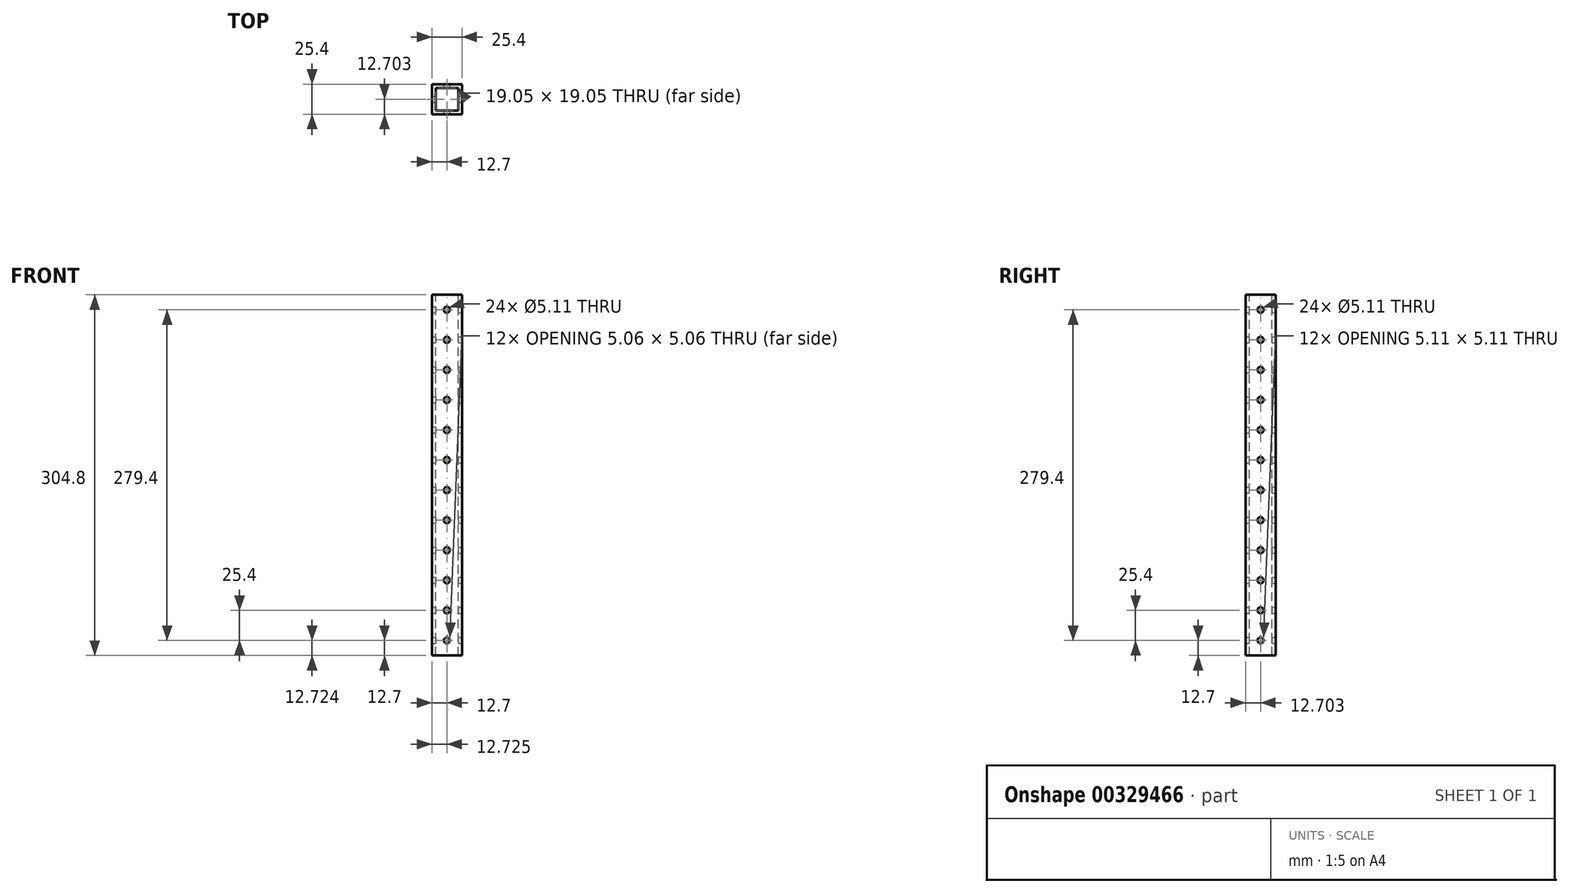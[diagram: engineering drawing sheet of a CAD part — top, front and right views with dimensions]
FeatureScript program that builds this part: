
annotation { "Feature Type Name" : "Feature", "Feature Type Description" : "" }
export const myFeature = defineFeature(function(context is Context, id is Id, definition is map)
    precondition{}
    {
        {
            var Q0;
            Q0=qCreatedBy(makeId("Right.planeOp"),FACE);
            var sketch = newSketch(context, id + "F0", { "sketchPlane" : qUnion([Q0])});
            skLineSegment(sketch, "E0.bottom", {"start": v(-26.89, 312.65) * mm, "end": v(-1.49, 312.65) * mm});
            skLineSegment(sketch, "E0.top", {"start": v(-26.89, 7.85) * mm, "end": v(-1.49, 7.85) * mm});
            skLineSegment(sketch, "E0.left", {"start": v(-26.89, 312.65) * mm, "end": v(-26.89, 7.85) * mm});
            skLineSegment(sketch, "E0.right", {"start": v(-1.49, 312.65) * mm, "end": v(-1.49, 7.85) * mm});
            skSolve(sketch);
        }
        {
            var Q0;
            Q0 = qSketchRegion(id + "F0", true);
            extrude(context, id + "F1", {"entities" : qUnion([Q0]), "depth" : 25.4 * mm});
        }
        {
            var Q0;
            Q0=makeQuery(id+"F1.opExtrude","SWEPT_FACE",FACE,{"disambiguationData":[OSD([sQuery(id+"F0.wireOp",EDGE,"E0.bottom")])]});
            var sketch = newSketch(context, id + "F2", { "sketchPlane" : qUnion([Q0])});
            skLineSegment(sketch, "E1.bottom", {"start": v(3.17, -4.66) * mm, "end": v(22.23, -4.66) * mm});
            skLineSegment(sketch, "E1.top", {"start": v(3.18, -23.71) * mm, "end": v(22.23, -23.71) * mm});
            skLineSegment(sketch, "E1.left", {"start": v(3.17, -4.66) * mm, "end": v(3.18, -23.71) * mm});
            skLineSegment(sketch, "E1.right", {"start": v(22.23, -4.66) * mm, "end": v(22.23, -23.71) * mm});
            skSolve(sketch);
        }
        {
            var Q0;
            Q0 = qSketchRegion(id + "F2", true);
            extrude(context, id + "F3", {"entities" : qUnion([Q0]), "operationType" : NewBodyOperationType.REMOVE, "oppositeDirection" : true, "depth" : 304.8 * mm});
        }
        {
            var Q0;
            Q0=makeQuery(id+"F1.opExtrude","CAP_FACE",FACE,{"disambiguationData":[OSD([sQuery(id+"F0.wireOp",EDGE,"E0.bottom"),sQuery(id+"F0.wireOp",EDGE,"E0.top"),sQuery(id+"F0.wireOp",EDGE,"E0.left"),sQuery(id+"F0.wireOp",EDGE,"E0.right")])],"isStart":false});
            var sketch = newSketch(context, id + "F4", { "sketchPlane" : qUnion([Q0])});
            skCircle(sketch, "E2", {"center": v(-14.19, 299.95) * mm, "radius": 2.55 * mm});
            skCircle(sketch, "E3.0.1.0", {"center": v(-14.19, 274.55) * mm, "radius": 2.55 * mm});
            skCircle(sketch, "E3.0.2.0", {"center": v(-14.19, 249.15) * mm, "radius": 2.55 * mm});
            skCircle(sketch, "E3.0.3.0", {"center": v(-14.19, 223.75) * mm, "radius": 2.55 * mm});
            skCircle(sketch, "E3.0.4.0", {"center": v(-14.19, 198.35) * mm, "radius": 2.55 * mm});
            skCircle(sketch, "E3.0.5.0", {"center": v(-14.19, 172.95) * mm, "radius": 2.55 * mm});
            skCircle(sketch, "E3.0.6.0", {"center": v(-14.19, 147.55) * mm, "radius": 2.55 * mm});
            skCircle(sketch, "E3.0.7.0", {"center": v(-14.19, 122.15) * mm, "radius": 2.55 * mm});
            skCircle(sketch, "E3.0.8.0", {"center": v(-14.19, 96.75) * mm, "radius": 2.55 * mm});
            skCircle(sketch, "E3.0.9.0", {"center": v(-14.19, 71.35) * mm, "radius": 2.55 * mm});
            skCircle(sketch, "E3.0.10.0", {"center": v(-14.19, 45.95) * mm, "radius": 2.55 * mm});
            skCircle(sketch, "E3.0.11.0", {"center": v(-14.19, 20.55) * mm, "radius": 2.55 * mm});
            skLineSegment(sketch, "E3.direction1", {"start": v(-14.19, 299.95) * mm, "end": v(11.21, 299.95) * mm, "construction": true});
            skLineSegment(sketch, "E3.direction2", {"start": v(-14.19, 299.95) * mm, "end": v(-14.19, 274.55) * mm, "construction": true});
            skSolve(sketch);
        }
        {
            var Q0;
            Q0=sQuery(id+"F4.wireOp",VERTEX,"E3.0.11.0.center");
            var Q1;
            Q1=sQuery(id+"F4.wireOp",VERTEX,"E3.0.8.0.center");
            var Q2;
            Q2=sQuery(id+"F4.wireOp",VERTEX,"E3.0.7.0.center");
            var Q3;
            Q3=sQuery(id+"F4.wireOp",VERTEX,"E3.0.6.0.center");
            var Q4;
            Q4=sQuery(id+"F4.wireOp",VERTEX,"E3.0.10.0.center");
            var Q5;
            Q5=sQuery(id+"F4.wireOp",VERTEX,"E3.0.9.0.center");
            var Q6;
            Q6=sQuery(id+"F4.wireOp",VERTEX,"E3.0.5.0.center");
            var Q7;
            Q7=sQuery(id+"F4.wireOp",VERTEX,"E3.direction1.start");
            var Q8;
            Q8=sQuery(id+"F4.wireOp",VERTEX,"E3.0.4.0.center");
            var Q9;
            Q9=sQuery(id+"F4.wireOp",VERTEX,"E3.0.3.0.center");
            var Q10;
            Q10=sQuery(id+"F4.wireOp",VERTEX,"E3.0.2.0.center");
            var Q11;
            Q11=sQuery(id+"F4.wireOp",VERTEX,"E3.0.1.0.center");
            var Q12;
            Q12=sQuery(id+"F4.wireOp",VERTEX,"E3.direction1.end");
            var Q13;
            Q13=makeQuery(id+"F1.opExtrude","SWEPT_BODY",BODY,{"disambiguationData":[OSD([sQuery(id+"F0.wireOp",EDGE,"E0.bottom"),sQuery(id+"F0.wireOp",EDGE,"E0.top"),sQuery(id+"F0.wireOp",EDGE,"E0.left"),sQuery(id+"F0.wireOp",EDGE,"E0.right")])]});
            hole(context, id + "F5", {"style" : HoleStyle.SIMPLE, "endStyle" : HoleEndStyle.BLIND, "holeDiameter" : 5.1 * mm, "holeDepth" : 25.4 * mm, "tappedDepth" : 12.7 * mm, "tapClearance" : 3, "startFromSketch" : true, "locations" : qUnion([Q0, Q1, Q2, Q3, Q4, Q5, Q6, Q7, Q8, Q9, Q10, Q11, Q12]), "scope" : qUnion([Q13])});
        }
        {
            var Q0;
            Q0=makeQuery(id+"F1.opExtrude","SWEPT_FACE",FACE,{"disambiguationData":[OSD([sQuery(id+"F0.wireOp",EDGE,"E0.right")])]});
            var sketch = newSketch(context, id + "F6", { "sketchPlane" : qUnion([Q0])});
            skCircle(sketch, "E4", {"center": v(-12.7, 299.95) * mm, "radius": 2.55 * mm});
            skCircle(sketch, "E5.0.1.0", {"center": v(-12.7, 274.55) * mm, "radius": 2.55 * mm});
            skCircle(sketch, "E5.0.2.0", {"center": v(-12.7, 249.15) * mm, "radius": 2.55 * mm});
            skCircle(sketch, "E5.0.3.0", {"center": v(-12.7, 223.75) * mm, "radius": 2.55 * mm});
            skCircle(sketch, "E5.0.4.0", {"center": v(-12.7, 198.35) * mm, "radius": 2.55 * mm});
            skCircle(sketch, "E5.0.5.0", {"center": v(-12.7, 172.95) * mm, "radius": 2.55 * mm});
            skCircle(sketch, "E5.0.6.0", {"center": v(-12.7, 147.55) * mm, "radius": 2.55 * mm});
            skCircle(sketch, "E5.0.7.0", {"center": v(-12.7, 122.15) * mm, "radius": 2.55 * mm});
            skCircle(sketch, "E5.0.8.0", {"center": v(-12.7, 96.75) * mm, "radius": 2.55 * mm});
            skCircle(sketch, "E5.0.9.0", {"center": v(-12.7, 71.35) * mm, "radius": 2.55 * mm});
            skCircle(sketch, "E5.0.10.0", {"center": v(-12.7, 45.95) * mm, "radius": 2.55 * mm});
            skCircle(sketch, "E5.0.11.0", {"center": v(-12.7, 20.55) * mm, "radius": 2.55 * mm});
            skLineSegment(sketch, "E5.direction1", {"start": v(-12.7, 299.95) * mm, "end": v(12.7, 299.95) * mm, "construction": true});
            skLineSegment(sketch, "E5.direction2", {"start": v(-12.7, 299.95) * mm, "end": v(-12.7, 274.55) * mm, "construction": true});
            skSolve(sketch);
        }
        {
            var Q0;
            Q0=sQuery(id+"F6.wireOp",VERTEX,"E5.0.11.0.center");
            var Q1;
            Q1=sQuery(id+"F6.wireOp",VERTEX,"E5.0.9.0.center");
            var Q2;
            Q2=sQuery(id+"F6.wireOp",VERTEX,"E5.0.10.0.center");
            var Q3;
            Q3=sQuery(id+"F6.wireOp",VERTEX,"E5.direction1.start");
            var Q4;
            Q4=sQuery(id+"F6.wireOp",VERTEX,"E5.0.2.0.center");
            var Q5;
            Q5=sQuery(id+"F6.wireOp",VERTEX,"E5.0.1.0.center");
            var Q6;
            Q6=sQuery(id+"F6.wireOp",VERTEX,"E5.0.7.0.center");
            var Q7;
            Q7=sQuery(id+"F6.wireOp",VERTEX,"E5.0.8.0.center");
            var Q8;
            Q8=sQuery(id+"F6.wireOp",VERTEX,"E5.0.5.0.center");
            var Q9;
            Q9=sQuery(id+"F6.wireOp",VERTEX,"E5.0.6.0.center");
            var Q10;
            Q10=sQuery(id+"F6.wireOp",VERTEX,"E5.0.3.0.center");
            var Q11;
            Q11=sQuery(id+"F6.wireOp",VERTEX,"E5.0.4.0.center");
            var Q12;
            Q12=makeQuery(id+"F1.opExtrude","SWEPT_BODY",BODY,{"disambiguationData":[OSD([sQuery(id+"F0.wireOp",EDGE,"E0.bottom"),sQuery(id+"F0.wireOp",EDGE,"E0.top"),sQuery(id+"F0.wireOp",EDGE,"E0.left"),sQuery(id+"F0.wireOp",EDGE,"E0.right")])]});
            hole(context, id + "F7", {"style" : HoleStyle.SIMPLE, "endStyle" : HoleEndStyle.BLIND, "holeDiameter" : 5.1 * mm, "holeDepth" : 25.4 * mm, "tappedDepth" : 12.7 * mm, "tapClearance" : 3, "startFromSketch" : true, "locations" : qUnion([Q0, Q1, Q2, Q3, Q4, Q5, Q6, Q7, Q8, Q9, Q10, Q11]), "scope" : qUnion([Q12])});
        }
    });
